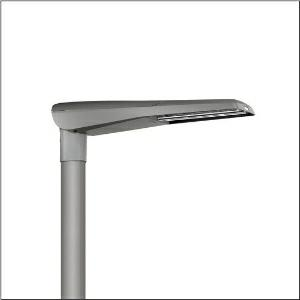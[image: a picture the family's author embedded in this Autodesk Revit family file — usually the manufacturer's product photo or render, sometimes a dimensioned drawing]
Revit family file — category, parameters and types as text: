
# Revit family: streetlight_sl_11_iq_mini___st1_2a_5xc2ac1g08ge_ba73
name_source: partatom
category: Lighting Fixtures
units: mm (PartAtom-declared; Revit-internal decimal feet)

## family parameters
Cut with Voids When Loaded = No
Host = Face
Light Source = No
Part Type = Normal
Room Calculation Point = No
Round Connector Dimension = Use Diameter
Shared = No

## types (1)
- --- (1 x LED, 3040 lm, 25.3 W, 2200K)
    Apparent Load = 25 VA
    CIE Flux Codes = 32 70 96 100 100
    Color Rendering = 70
    Color Temperature = 2200K
    Default Elevation = 1800 mm
    Description = Streetlight SL 11 iQ mini, mast luminaire, primary light control with 3 zone facetted reflector, of plastic, silver coated, highly specular, primary optical cover: cover, of PMMA, transparent, light distribution: ST1.2a, light emission: direct distribution, primary light characteristic: asymmetric, installation type: post-top, side-entry, lamps: LED, High Power LED, rated values: 3.570lm | 24,9W | 143,4lm/W (begin service life); end service life: 3.570lm | 25,7W; at 50% lumin. flux: 1.785lm | 12,8W | 139,5lm/W, colour temperature: 2200/2700/3000/4000K, colour rendering: CRI > 70, light colour: 722/727/730/740, light setting 1 begin service life: 100% | 3.570lm | 24,9W | 143,4lm/W | 3.000K, light setting 1 end service life: 25,7W, further light settings possible, control: pre-setting: linear dimming characteristic, Street-Remote, Auto-Match, Temp-Guard, Lumen-Switch, Night-Set, Smart-Wire, Light-Fading, Desk-Remote (wireless, voltage-free reading and setting of iQ features in the workshop via application-optimized NFC function/RFID function), optimised constant luminous flux control (CLO 2.0), with cable H07RN-F 5x 1.5mm², mains connection: 230..240V, AC, 50/60Hz, connection cable pre-assembled, cable length: 6,5m, luminaire housing, of diecast aluminium, powder-coated, Siteco® metallic grey (DB 702S), please order mast flange separately, inclination adjustable without tools: 0°, 5°, 10°, 15° (post-top) | 0°, -5°, -10°, -15° (side-entry), sealing non-destructively replaceable, multi-level sealing system, length: 736mm, width: 174mm, height: 116mm, mast flange for spigot size: 42mm (side-entry): 5XC10008XM4, 60/48mm (side-entry/post-top): 5XC10108XM2, 76/60mm (side-entry/post-top): 5XC10108XM1, equipment: standard, protection rating (complete): IP66, insulation class (complete): insulation class II (safety insulation), certification: CE, ENEC, ENEC+, VDE, impact resistance: IK10, permissible operating ambient temperature for outdoor applications: -25..+50°C, standard-compliant lighting for roads and squares, Environmental Product Declaration (EPD) tested and certified by an independent institute, packaging unit: 1 piece

Light Distribution: ST1.2a
    Height = 116 mm
    Lamp = 1 x LED
    Lamp Light Flux = 3040 lm
    Lamp Power = 25.3 W
    Lamp count = 1
    Length = 736 mm
    Luminous efficacy = 120 lm/W
    Manufacturer = Siteco
    ModVariant = No
    Model = 5XC2AC1G08GE
    Number of Poles = 1
    OnlyDefault = Yes
    Power Factor = 1
    Product Name = Streetlight SL 11 iQ mini | ST1.2a
    Product group = mast luminaire | pylon top
    ProductGroupID = 6100
    Protection Class = Protection class II
    Protection Degree = IP 66
    RLX_Detail_Level = 1
    RLX_Emergency_Light_Flux = 0 lm
    RLX_Emergency_Type = 0
    RLX_Emergency_Type_DB = No
    RlxData = <blob elided: 53641 chars, md5=24a2421e>
    Socket = socket
    Standby Power = 0 W
    System Light Flux = 3040 lm
    System Power = 25 W
    Type Comments = individual setting: luminous flux: 100 % | dim-lin: 254 | 351 mA
    Type Image = l_1003508.jpg
    URL = http://relux.com
    VarID = @adj_055515
    Voltage = 0 V
    Weight = 0.00 kg
    Width = 174 mm

## geometry (parser evidence)
native form markers: Blend x4, Sweep x10
no freeform markers — native parametric forms only
